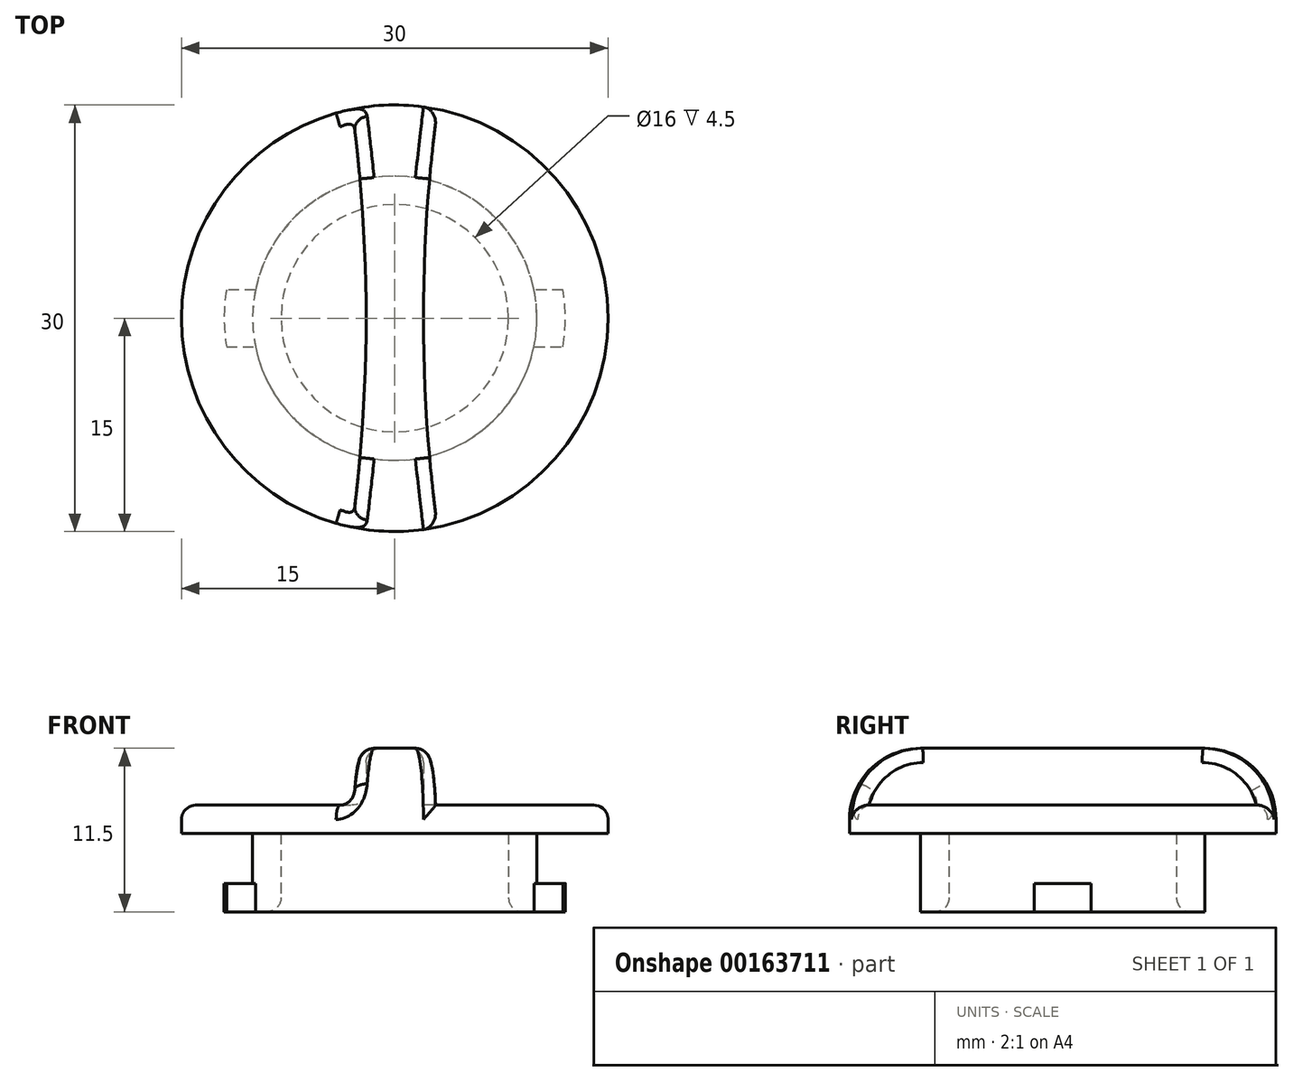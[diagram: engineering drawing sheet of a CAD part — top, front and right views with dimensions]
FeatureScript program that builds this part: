
annotation { "Feature Type Name" : "Feature", "Feature Type Description" : "" }
export const myFeature = defineFeature(function(context is Context, id is Id, definition is map)
    precondition{}
    {
        {
            var Q0;
            Q0=qCreatedBy(makeId("Top.planeOp"),FACE);
            var sketch = newSketch(context, id + "F0", { "sketchPlane" : qUnion([Q0])});
            skCircle(sketch, "E0", {"center": v(0, 0) * mm, "radius": 10 * mm});
            skCircle(sketch, "E1", {"center": v(0, 0) * mm, "radius": 8 * mm});
            skSolve(sketch);
        }
        {
            var Q0;
            Q0 = qSketchRegion(id + "F0", true);
            extrude(context, id + "F1", {"entities" : qUnion([Q0]), "depth" : 5.5 * mm});
        }
        {
            var Q0;
            Q0=makeQuery(id+"F1.opExtrude","CAP_FACE",FACE,{"disambiguationData":[OSD([sQuery(id+"F0.wireOp",EDGE,"E0"),sQuery(id+"F0.wireOp",EDGE,"E1")])],"isStart":false});
            var sketch = newSketch(context, id + "F2", { "sketchPlane" : qUnion([Q0])});
            skCircle(sketch, "E2", {"center": v(0, 0) * mm, "radius": 15 * mm});
            skSolve(sketch);
        }
        {
            var Q0;
            Q0 = qSketchRegion(id + "F2", true);
            extrude(context, id + "F3", {"entities" : qUnion([Q0]), "operationType" : NewBodyOperationType.ADD, "depth" : 2 * mm});
        }
        {
            var Q0;
            Q0=makeQuery(id+"F3.opExtrude","CAP_FACE",FACE,{"disambiguationData":[OSD([sQuery(id+"F2.wireOp",EDGE,"E2")])],"isStart":false});
            var sketch = newSketch(context, id + "F4", { "sketchPlane" : qUnion([Q0])});
            skLineSegment(sketch, "E3", {"start": v(0, 0) * mm, "end": v(0, 18.12) * mm, "construction": true});
            skLineSegment(sketch, "E4", {"start": v(-3, 14.7) * mm, "end": v(-3, -14.7) * mm, "construction": true});
            skLineSegment(sketch, "E5", {"start": v(3, -14.7) * mm, "end": v(3, 14.7) * mm, "construction": true});
            skArc(sketch, "E6", {"start": v(-3, 14.7) * mm, "mid": v(0, 15) * mm, "end": v(3, 14.7) * mm});
            skArc(sketch, "E7", {"start": v(-3, -14.7) * mm, "mid": v(0, -15) * mm, "end": v(3, -14.7) * mm});
            skArc(sketch, "E8", {"start": v(-3, 14.7) * mm, "mid": v(-2.01, 0) * mm, "end": v(-3, -14.7) * mm});
            skArc(sketch, "E9.MirrorCS", {"start": v(3, 14.7) * mm, "mid": v(2.01, 0) * mm, "end": v(3, -14.7) * mm});
            skSolve(sketch);
        }
        {
            var Q0;
            Q0 = qSketchRegion(id + "F4", true);
            extrude(context, id + "F5", {"entities" : qUnion([Q0]), "operationType" : NewBodyOperationType.ADD, "depth" : 4 * mm});
        }
        {
            var Q0;
            Q0=makeQuery(id+"F5.opExtrude","CAP_EDGE",EDGE,{"disambiguationData":[OSD([sQuery(id+"F4.wireOp",EDGE,"E7")])],"isStart":false});
            fillet(context, id + "F6", {"entities" : qUnion([Q0]), "radius" : 5 * mm, "tangentPropagation" : true, "allowEdgeOverflow" : false});
        }
        {
            var Q0;
            Q0=makeQuery(id+"F1.opExtrude","CAP_FACE",FACE,{"disambiguationData":[OSD([sQuery(id+"F0.wireOp",EDGE,"E0"),sQuery(id+"F0.wireOp",EDGE,"E1")])],"isStart":true});
            var sketch = newSketch(context, id + "F7", { "sketchPlane" : qUnion([Q0])});
            skLineSegment(sketch, "E10", {"start": v(-11.83, 2) * mm, "end": v(-7.75, 2) * mm});
            skLineSegment(sketch, "E11", {"start": v(11.83, -2) * mm, "end": v(7.75, -2) * mm});
            skArc(sketch, "E12", {"start": v(-11.83, 2) * mm, "mid": v(-12, 0) * mm, "end": v(-11.83, -2) * mm});
            skArc(sketch, "E13", {"start": v(11.83, 2) * mm, "mid": v(12, 0) * mm, "end": v(11.83, -2) * mm});
            skArc(sketch, "E14", {"start": v(-7.75, 2) * mm, "mid": v(-8, 0) * mm, "end": v(-7.75, -2) * mm});
            skArc(sketch, "E15", {"start": v(7.75, 2) * mm, "mid": v(8, 0) * mm, "end": v(7.75, -2) * mm});
            skLineSegment(sketch, "E16.trimOffspring", {"start": v(7.75, 2) * mm, "end": v(11.83, 2) * mm});
            skLineSegment(sketch, "E17.trimOffspring", {"start": v(-7.75, -2) * mm, "end": v(-11.83, -2) * mm});
            skSolve(sketch);
        }
        {
            var Q0;
            Q0 = qSketchRegion(id + "F7", true);
            extrude(context, id + "F8", {"entities" : qUnion([Q0]), "operationType" : NewBodyOperationType.ADD, "oppositeDirection" : true, "depth" : 2 * mm});
        }
        {
            var Q0;
            Q0=makeQuery(id+"F5.opExtrude","CAP_EDGE",EDGE,{"disambiguationData":[OSD([sQuery(id+"F4.wireOp",EDGE,"E8")])],"isStart":false});
            var Q1;
            Q1=makeQuery(id+"F5.opExtrude","CAP_EDGE",EDGE,{"disambiguationData":[OSD([sQuery(id+"F4.wireOp",EDGE,"E9.MirrorCS")])],"isStart":false});
            var Q2;
            {var subQ0=sQuery(id+"F2.wireOp",EDGE,"E2");var subQ1=sQuery(id+"F4.wireOp",EDGE,"E7");Q2=makeQuery(id+"F6.opFillet","BLEND_EDGE",EDGE,{"blendedFrom":[makeQuery(id+"F5.opExtrude","CAP_EDGE",EDGE,{"disambiguationData":[OSD([subQ1])],"isStart":false}),makeQuery(id+"F5.boolean.opBoolean","SPLIT",FACE,{"disambiguationData":[TD([makeQuery(id+"F5.opExtrude","SWEPT_FACE",FACE,{"disambiguationData":[OSD([sQuery(id+"F4.wireOp",EDGE,"E9.MirrorCS")])]})])],"derivedFrom":makeQuery(id+"F3.opExtrude","CAP_FACE",FACE,{"disambiguationData":[OSD([subQ0])],"isStart":false})})],"blendedInto":[makeQuery(id+"F5.boolean.opBoolean","SPLIT",FACE,{"disambiguationData":[TD([makeQuery(id+"F5.opExtrude","SWEPT_FACE",FACE,{"disambiguationData":[OSD([sQuery(id+"F4.wireOp",EDGE,"E9.MirrorCS")])]})])],"derivedFrom":makeQuery(id+"F3.opExtrude","CAP_FACE",FACE,{"disambiguationData":[OSD([subQ0])],"isStart":false})})]});}
            var Q3;
            {var subQ0=sQuery(id+"F2.wireOp",EDGE,"E2");var subQ1=sQuery(id+"F4.wireOp",EDGE,"E7");Q3=makeQuery(id+"F6.opFillet","BLEND_EDGE",EDGE,{"blendedFrom":[makeQuery(id+"F5.opExtrude","CAP_EDGE",EDGE,{"disambiguationData":[OSD([subQ1])],"isStart":false}),makeQuery(id+"F5.boolean.opBoolean","SPLIT",FACE,{"disambiguationData":[TD([makeQuery(id+"F5.opExtrude","SWEPT_FACE",FACE,{"disambiguationData":[OSD([sQuery(id+"F4.wireOp",EDGE,"E8")])]})])],"derivedFrom":makeQuery(id+"F3.opExtrude","CAP_FACE",FACE,{"disambiguationData":[OSD([subQ0])],"isStart":false})})],"blendedInto":[makeQuery(id+"F5.boolean.opBoolean","SPLIT",FACE,{"disambiguationData":[TD([makeQuery(id+"F5.opExtrude","SWEPT_FACE",FACE,{"disambiguationData":[OSD([sQuery(id+"F4.wireOp",EDGE,"E8")])]})])],"derivedFrom":makeQuery(id+"F3.opExtrude","CAP_FACE",FACE,{"disambiguationData":[OSD([subQ0])],"isStart":false})})]});}
            var Q4;
            Q4=makeQuery(id+"F5.opExtrude","CAP_EDGE",EDGE,{"disambiguationData":[OSD([sQuery(id+"F4.wireOp",EDGE,"E8")])],"isStart":true});
            var Q5;
            Q5=makeQuery(id+"F5.opExtrude","CAP_EDGE",EDGE,{"disambiguationData":[OSD([sQuery(id+"F4.wireOp",EDGE,"E9.MirrorCS")])],"isStart":true});
            var Q6;
            Q6=makeQuery(id+"F1.opExtrude","CAP_EDGE",EDGE,{"disambiguationData":[OSD([sQuery(id+"F0.wireOp",EDGE,"E1")])],"isStart":true});
            fillet(context, id + "F9", {"entities" : qUnion([Q0, Q1, Q2, Q3, Q4, Q5, Q6]), "radius" : 1 * mm, "tangentPropagation" : true, "allowEdgeOverflow" : false});
        }
    });
